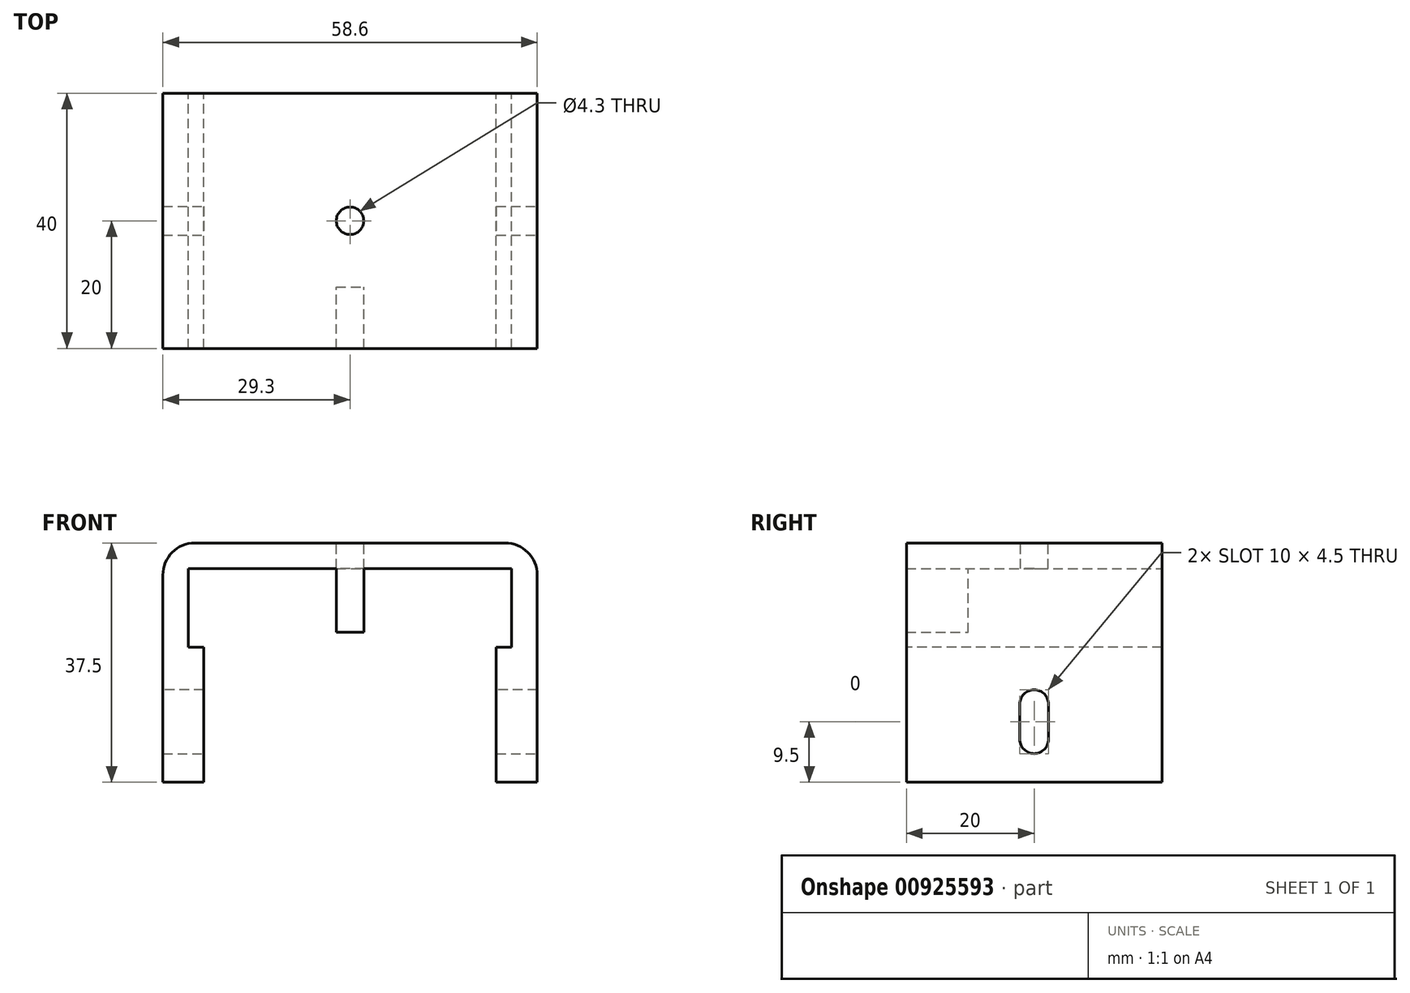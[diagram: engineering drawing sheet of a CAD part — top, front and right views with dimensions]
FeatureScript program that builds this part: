
annotation { "Feature Type Name" : "Feature", "Feature Type Description" : "" }
export const myFeature = defineFeature(function(context is Context, id is Id, definition is map)
    precondition{}
    {
        {
            var Q0;
            Q0=qCreatedBy(makeId("Front.planeOp"),FACE);
            var sketch = newSketch(context, id + "F0", { "sketchPlane" : qUnion([Q0])});
            skLineSegment(sketch, "E0.bottom", {"start": v(29.3, -18.75) * mm, "end": v(25.3, -18.75) * mm});
            skLineSegment(sketch, "E0.top", {"start": v(29.3, 18.75) * mm, "end": v(-29.3, 18.75) * mm});
            skLineSegment(sketch, "E0.left", {"start": v(29.3, -18.75) * mm, "end": v(29.3, 18.75) * mm});
            skLineSegment(sketch, "E0.right", {"start": v(-29.3, -18.75) * mm, "end": v(-29.3, 18.75) * mm});
            skPoint(sketch, "E0.middle", {"position": v(0, 0) * mm});
            skLineSegment(sketch, "E1.0", {"start": v(25.3, -18.75) * mm, "end": v(25.3, 14.75) * mm});
            skLineSegment(sketch, "E1.1", {"start": v(25.3, 14.75) * mm, "end": v(-25.3, 14.75) * mm});
            skLineSegment(sketch, "E1.2", {"start": v(-25.3, -18.75) * mm, "end": v(-25.3, 14.75) * mm});
            skLineSegment(sketch, "E2.trimOffspring", {"start": v(-25.3, -18.75) * mm, "end": v(-29.3, -18.75) * mm});
            skSolve(sketch);
        }
        {
            var Q0;
            Q0 = qSketchRegion(id + "F0", true);
            extrude(context, id + "F1", {"entities" : qUnion([Q0]), "depth" : 40 * mm, "offsetDistance" : 25 * mm});
        }
        {
            var Q0;
            Q0=makeQuery(id+"F1.opExtrude","SWEPT_EDGE",EDGE,{"disambiguationData":[OSD([sQuery(id+"F0.wireOp",EDGE,"E0.top"),sQuery(id+"F0.wireOp",EDGE,"E0.right")])]});
            var Q1;
            Q1=makeQuery(id+"F1.opExtrude","SWEPT_EDGE",EDGE,{"disambiguationData":[OSD([sQuery(id+"F0.wireOp",EDGE,"E0.top"),sQuery(id+"F0.wireOp",EDGE,"E0.left")])]});
            fillet(context, id + "F2", {"entities" : qUnion([Q0, Q1]), "radius" : 5 * mm, "tangentPropagation" : true, "allowEdgeOverflow" : false});
        }
        {
            var Q0;
            Q0=makeQuery(id+"F1.opExtrude","SWEPT_FACE",FACE,{"disambiguationData":[OSD([sQuery(id+"F0.wireOp",EDGE,"E0.top")])]});
            var sketch = newSketch(context, id + "F3", { "sketchPlane" : qUnion([Q0])});
            skCircle(sketch, "E3", {"center": v(0, -20) * mm, "radius": 2.15 * mm});
            skPoint(sketch, "E3.centerSnap0", {"position": v(24.3, -20) * mm});
            skSolve(sketch);
        }
        {
            var Q0;
            Q0 = qSketchRegion(id + "F3", true);
            extrude(context, id + "F4", {"entities" : qUnion([Q0]), "operationType" : NewBodyOperationType.REMOVE, "oppositeDirection" : true, "depth" : 25 * mm, "offsetDistance" : 25 * mm});
        }
        {
            var Q0;
            Q0=makeQuery(id+"F1.opExtrude","SWEPT_FACE",FACE,{"disambiguationData":[OSD([sQuery(id+"F0.wireOp",EDGE,"E0.left")])]});
            var sketch = newSketch(context, id + "F5", { "sketchPlane" : qUnion([Q0])});
            skLineSegment(sketch, "E4.bottom", {"start": v(-17.75, -14.25) * mm, "end": v(-22.25, -14.25) * mm});
            skLineSegment(sketch, "E4.top", {"start": v(-17.75, -4.25) * mm, "end": v(-22.25, -4.25) * mm});
            skLineSegment(sketch, "E4.left", {"start": v(-17.75, -14.25) * mm, "end": v(-17.75, -4.25) * mm});
            skLineSegment(sketch, "E4.right", {"start": v(-22.25, -14.25) * mm, "end": v(-22.25, -4.25) * mm});
            skPoint(sketch, "E4.middle", {"position": v(-20, -9.25) * mm});
            skPoint(sketch, "E4.middle.positionSnap0", {"position": v(-20, -18.75) * mm});
            skPoint(sketch, "E4.centerSnap0", {"position": v(-20, -18.75) * mm});
            skSolve(sketch);
        }
        {
            var Q0;
            Q0 = qSketchRegion(id + "F5", true);
            extrude(context, id + "F6", {"entities" : qUnion([Q0]), "operationType" : NewBodyOperationType.REMOVE, "endBound" : BoundingType.THROUGH_ALL, "oppositeDirection" : true, "depth" : 25 * mm, "offsetDistance" : 25 * mm});
        }
        {
            var Q0;
            {var subQ0=sQuery(id+"F5.wireOp",EDGE,"E4.top");var subQ1=sQuery(id+"F5.wireOp",EDGE,"E4.left");Q0=makeQuery(id+"F6.boolean.opBoolean","COPY",EDGE,{"disambiguationData":[TD([makeQuery(id+"F1.opExtrude","SWEPT_FACE",FACE,{"disambiguationData":[OSD([sQuery(id+"F0.wireOp",EDGE,"E0.left")])]})])],"derivedFrom":makeQuery(id+"F6.opExtrude","SWEPT_EDGE",EDGE,{"disambiguationData":[OSD([subQ0,subQ1])]})});}
            var Q1;
            {var subQ0=sQuery(id+"F5.wireOp",EDGE,"E4.right");var subQ1=sQuery(id+"F5.wireOp",EDGE,"E4.top");Q1=makeQuery(id+"F6.boolean.opBoolean","COPY",EDGE,{"disambiguationData":[TD([makeQuery(id+"F1.opExtrude","SWEPT_FACE",FACE,{"disambiguationData":[OSD([sQuery(id+"F0.wireOp",EDGE,"E0.left")])]})])],"derivedFrom":makeQuery(id+"F6.opExtrude","SWEPT_EDGE",EDGE,{"disambiguationData":[OSD([subQ1,subQ0])]})});}
            var Q2;
            {var subQ0=sQuery(id+"F5.wireOp",EDGE,"E4.bottom");var subQ1=sQuery(id+"F5.wireOp",EDGE,"E4.left");Q2=makeQuery(id+"F6.boolean.opBoolean","COPY",EDGE,{"disambiguationData":[TD([makeQuery(id+"F1.opExtrude","SWEPT_FACE",FACE,{"disambiguationData":[OSD([sQuery(id+"F0.wireOp",EDGE,"E0.left")])]})])],"derivedFrom":makeQuery(id+"F6.opExtrude","SWEPT_EDGE",EDGE,{"disambiguationData":[OSD([subQ0,subQ1])]})});}
            var Q3;
            {var subQ0=sQuery(id+"F5.wireOp",EDGE,"E4.bottom");var subQ1=sQuery(id+"F5.wireOp",EDGE,"E4.right");Q3=makeQuery(id+"F6.boolean.opBoolean","COPY",EDGE,{"disambiguationData":[TD([makeQuery(id+"F1.opExtrude","SWEPT_FACE",FACE,{"disambiguationData":[OSD([sQuery(id+"F0.wireOp",EDGE,"E0.left")])]})])],"derivedFrom":makeQuery(id+"F6.opExtrude","SWEPT_EDGE",EDGE,{"disambiguationData":[OSD([subQ0,subQ1])]})});}
            var Q4;
            {var subQ0=sQuery(id+"F5.wireOp",EDGE,"E4.left");var subQ1=sQuery(id+"F5.wireOp",EDGE,"E4.top");Q4=makeQuery(id+"F6.boolean.opBoolean","COPY",EDGE,{"disambiguationData":[TD([makeQuery(id+"F1.opExtrude","SWEPT_FACE",FACE,{"disambiguationData":[OSD([sQuery(id+"F0.wireOp",EDGE,"E0.right")])]})])],"derivedFrom":makeQuery(id+"F6.opExtrude","SWEPT_EDGE",EDGE,{"disambiguationData":[OSD([subQ1,subQ0])]})});}
            var Q5;
            {var subQ0=sQuery(id+"F5.wireOp",EDGE,"E4.left");var subQ1=sQuery(id+"F5.wireOp",EDGE,"E4.bottom");Q5=makeQuery(id+"F6.boolean.opBoolean","COPY",EDGE,{"disambiguationData":[TD([makeQuery(id+"F1.opExtrude","SWEPT_FACE",FACE,{"disambiguationData":[OSD([sQuery(id+"F0.wireOp",EDGE,"E0.right")])]})])],"derivedFrom":makeQuery(id+"F6.opExtrude","SWEPT_EDGE",EDGE,{"disambiguationData":[OSD([subQ1,subQ0])]})});}
            var Q6;
            {var subQ0=sQuery(id+"F5.wireOp",EDGE,"E4.top");var subQ1=sQuery(id+"F5.wireOp",EDGE,"E4.right");Q6=makeQuery(id+"F6.boolean.opBoolean","COPY",EDGE,{"disambiguationData":[TD([makeQuery(id+"F1.opExtrude","SWEPT_FACE",FACE,{"disambiguationData":[OSD([sQuery(id+"F0.wireOp",EDGE,"E0.right")])]})])],"derivedFrom":makeQuery(id+"F6.opExtrude","SWEPT_EDGE",EDGE,{"disambiguationData":[OSD([subQ0,subQ1])]})});}
            var Q7;
            {var subQ0=sQuery(id+"F5.wireOp",EDGE,"E4.bottom");var subQ1=sQuery(id+"F5.wireOp",EDGE,"E4.right");Q7=makeQuery(id+"F6.boolean.opBoolean","COPY",EDGE,{"disambiguationData":[TD([makeQuery(id+"F1.opExtrude","SWEPT_FACE",FACE,{"disambiguationData":[OSD([sQuery(id+"F0.wireOp",EDGE,"E0.right")])]})])],"derivedFrom":makeQuery(id+"F6.opExtrude","SWEPT_EDGE",EDGE,{"disambiguationData":[OSD([subQ0,subQ1])]})});}
            fillet(context, id + "F7", {"entities" : qUnion([Q0, Q1, Q2, Q3, Q4, Q5, Q6, Q7]), "radius" : 2.25 * mm, "tangentPropagation" : true, "allowEdgeOverflow" : false});
        }
        {
            var Q0;
            Q0=makeQuery(id+"F1.opExtrude","SWEPT_FACE",FACE,{"disambiguationData":[OSD([sQuery(id+"F0.wireOp",EDGE,"E1.0")])]});
            var sketch = newSketch(context, id + "F8", { "sketchPlane" : qUnion([Q0])});
            skLineSegment(sketch, "E5.0", {"start": v(40, 2.45) * mm, "end": v(0, 2.45) * mm});
            skArc(sketch, "E6.0", {"start": v(22.25, -6.5) * mm, "mid": v(20, -4.25) * mm, "end": v(17.75, -6.5) * mm});
            skLineSegment(sketch, "E6.1", {"start": v(17.75, -12) * mm, "end": v(17.75, -6.5) * mm});
            skLineSegment(sketch, "E6.2", {"start": v(22.25, -12) * mm, "end": v(22.25, -6.5) * mm});
            skArc(sketch, "E6.3", {"start": v(17.75, -12) * mm, "mid": v(20, -14.25) * mm, "end": v(22.25, -12) * mm});
            skLineSegment(sketch, "E7.0", {"start": v(40, -18.75) * mm, "end": v(0, -18.75) * mm});
            skLineSegment(sketch, "E8", {"start": v(40, 2.45) * mm, "end": v(40, -18.75) * mm});
            skLineSegment(sketch, "E9", {"start": v(0, 2.45) * mm, "end": v(0, -18.75) * mm});
            skSolve(sketch);
        }
        {
            var Q0;
            Q0 = qSketchRegion(id + "F8", true);
            extrude(context, id + "F9", {"entities" : qUnion([Q0]), "operationType" : NewBodyOperationType.ADD, "depth" : 2.4 * mm, "offsetDistance" : 25 * mm});
        }
        {
            var Q0;
            Q0=makeQuery(id+"F1.opExtrude","SWEPT_FACE",FACE,{"disambiguationData":[OSD([sQuery(id+"F0.wireOp",EDGE,"E1.2")])]});
            var sketch = newSketch(context, id + "F10", { "sketchPlane" : qUnion([Q0])});
            skLineSegment(sketch, "E10.0", {"start": v(0, 2.45) * mm, "end": v(-40, 2.45) * mm});
            skArc(sketch, "E11.0", {"start": v(-17.75, -6.5) * mm, "mid": v(-20, -4.25) * mm, "end": v(-22.25, -6.5) * mm});
            skLineSegment(sketch, "E11.1", {"start": v(-22.25, -6.5) * mm, "end": v(-22.25, -12) * mm});
            skLineSegment(sketch, "E11.2", {"start": v(-17.75, -6.5) * mm, "end": v(-17.75, -12) * mm});
            skArc(sketch, "E11.3", {"start": v(-22.25, -12) * mm, "mid": v(-20, -14.25) * mm, "end": v(-17.75, -12) * mm});
            skLineSegment(sketch, "E12.0", {"start": v(-40, -18.75) * mm, "end": v(0, -18.75) * mm});
            skLineSegment(sketch, "E13", {"start": v(0, 2.45) * mm, "end": v(0, -18.75) * mm});
            skLineSegment(sketch, "E14", {"start": v(-40, 2.45) * mm, "end": v(-40, -18.75) * mm});
            skSolve(sketch);
        }
        {
            var Q0;
            Q0 = qSketchRegion(id + "F10", true);
            extrude(context, id + "F11", {"entities" : qUnion([Q0]), "operationType" : NewBodyOperationType.ADD, "depth" : 2.4 * mm, "offsetDistance" : 25 * mm});
        }
        {
            var Q0;
            Q0=makeQuery(id+"F1.opExtrude","SWEPT_FACE",FACE,{"disambiguationData":[OSD([sQuery(id+"F0.wireOp",EDGE,"E1.1")])]});
            var sketch = newSketch(context, id + "F12", { "sketchPlane" : qUnion([Q0])});
            skCircle(sketch, "E15.0", {"center": v(0, 20) * mm, "radius": 2.15 * mm, "construction": true});
            skLineSegment(sketch, "E16", {"start": v(-2.15, 20) * mm, "end": v(2.15, 20) * mm, "construction": true});
            skLineSegment(sketch, "E17.bottom", {"start": v(-2.15, 40) * mm, "end": v(2.15, 40) * mm});
            skLineSegment(sketch, "E17.top", {"start": v(-2.15, 30.35) * mm, "end": v(2.15, 30.35) * mm});
            skLineSegment(sketch, "E17.left", {"start": v(-2.15, 40) * mm, "end": v(-2.15, 30.35) * mm});
            skLineSegment(sketch, "E17.right", {"start": v(2.15, 40) * mm, "end": v(2.15, 30.35) * mm});
            skSolve(sketch);
        }
        {
            var Q0;
            Q0 = qSketchRegion(id + "F12", true);
            extrude(context, id + "F13", {"entities" : qUnion([Q0]), "operationType" : NewBodyOperationType.ADD, "depth" : 10 * mm, "offsetDistance" : 25 * mm});
        }
    });
